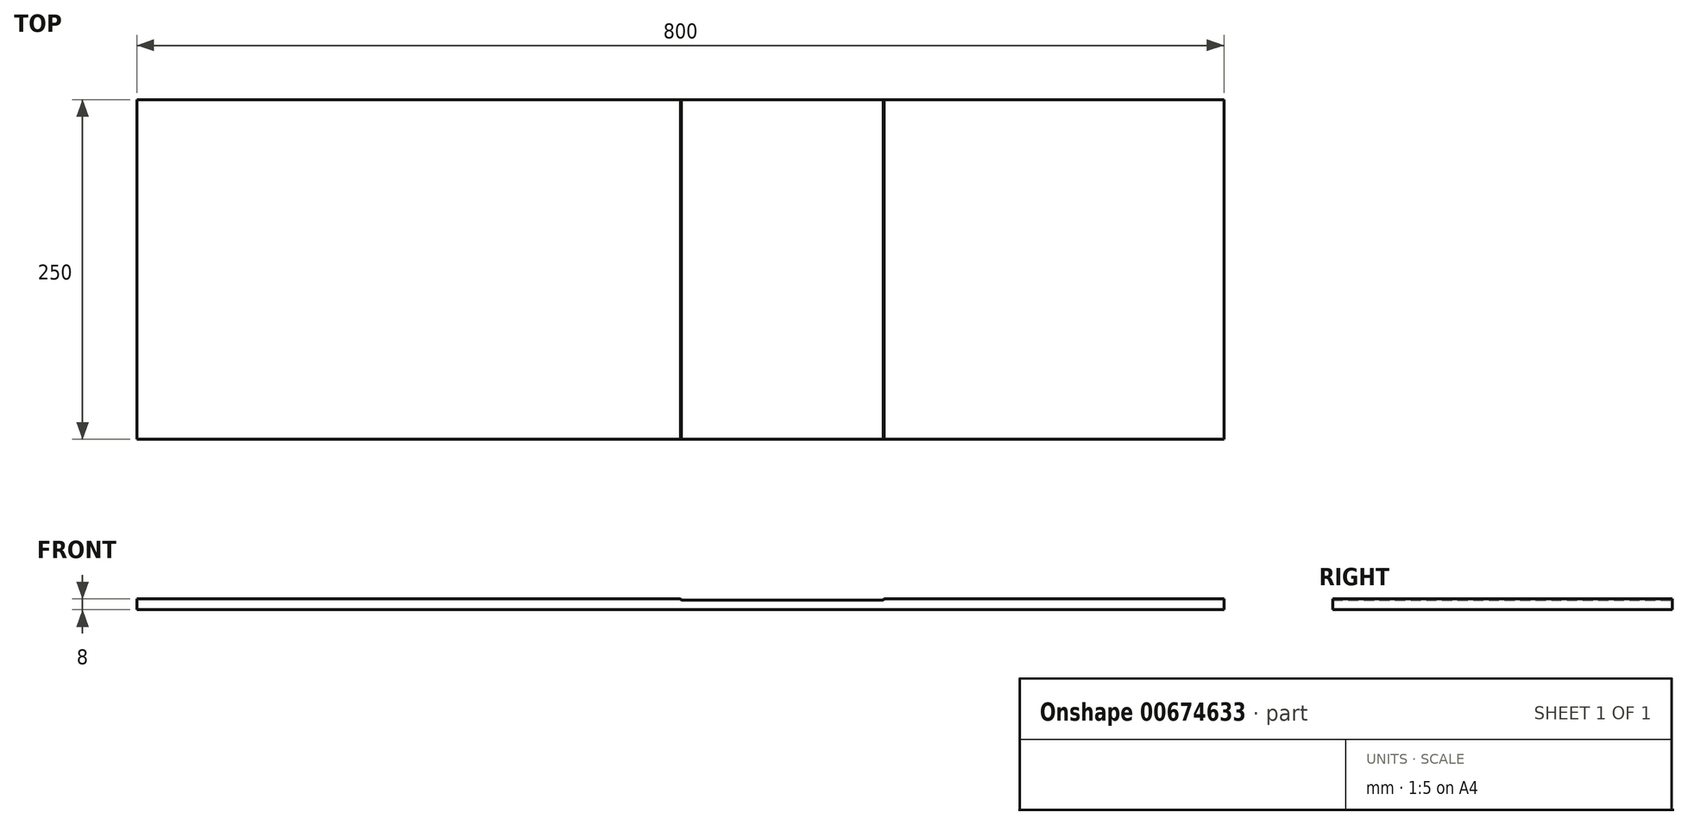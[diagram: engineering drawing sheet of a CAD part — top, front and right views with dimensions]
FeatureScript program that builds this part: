
annotation { "Feature Type Name" : "Feature", "Feature Type Description" : "" }
export const myFeature = defineFeature(function(context is Context, id is Id, definition is map)
    precondition{}
    {
        {
            var Q0;
            Q0=qCreatedBy(makeId("Front.planeOp"),FACE);
            var sketch = newSketch(context, id + "F0", { "sketchPlane" : qUnion([Q0])});
            skLineSegment(sketch, "E0", {"start": v(-225, 8) * mm, "end": v(575, 8) * mm});
            skLineSegment(sketch, "E1", {"start": v(575, 0) * mm, "end": v(-225, 0) * mm});
            skLineSegment(sketch, "E2", {"start": v(-225, 0) * mm, "end": v(-225, 8) * mm});
            skLineSegment(sketch, "E3", {"start": v(575, 0) * mm, "end": v(575, 8) * mm});
            skPoint(sketch, "E4", {"position": v(0, 0) * mm});
            skPoint(sketch, "E5", {"position": v(0, 8) * mm});
            skSolve(sketch);
        }
        {
            var Q0;
            Q0=qCreatedBy(makeId("Front.planeOp"),FACE);
            var sketch = newSketch(context, id + "F1", { "sketchPlane" : qUnion([Q0])});
            skLineSegment(sketch, "E6", {"start": v(175, 8) * mm, "end": v(175.7, 7) * mm});
            skLineSegment(sketch, "E7", {"start": v(250, 8) * mm, "end": v(175, 8) * mm});
            skLineSegment(sketch, "E8", {"start": v(175.7, 7) * mm, "end": v(250, 7) * mm});
            skLineSegment(sketch, "E9", {"start": v(250, 7) * mm, "end": v(250, 8) * mm, "construction": true});
            skLineSegment(sketch, "E10.MirrorCS", {"start": v(325, 8) * mm, "end": v(324.3, 7) * mm});
            skLineSegment(sketch, "E11.MirrorCS", {"start": v(250, 8) * mm, "end": v(325, 8) * mm});
            skLineSegment(sketch, "E12.MirrorCS", {"start": v(324.3, 7) * mm, "end": v(250, 7) * mm});
            skSolve(sketch);
        }
        {
            var Q0;
            Q0=qSketchRegion(id+"F0",true);
            extrude(context, id + "F2", {"entities" : qUnion([Q0]), "oppositeDirection" : true, "depth" : 250 * mm, "offsetDistance" : 25 * mm, "symmetric" : true});
        }
        {
            var Q0;
            Q0=qSketchRegion(id+"F1",true);
            var Q1;
            Q1=makeQuery(id+"F2.opExtrude","CAP_FACE",FACE,{"disambiguationData":[OSD([sQuery(id+"F0.wireOp",EDGE,"E0"),sQuery(id+"F0.wireOp",EDGE,"E1"),sQuery(id+"F0.wireOp",EDGE,"E2"),sQuery(id+"F0.wireOp",EDGE,"E3")])],"isStart":true});
            extrude(context, id + "F3", {"entities" : qUnion([Q0]), "operationType" : NewBodyOperationType.REMOVE, "endBound" : BoundingType.THROUGH_ALL, "depth" : 25 * mm, "endBoundEntityFace" : qUnion([Q1]), "offsetDistance" : 25 * mm});
        }
        {
            var Q0;
            Q0=qSketchRegion(id+"F1",true);
            extrude(context, id + "F4", {"entities" : qUnion([Q0]), "operationType" : NewBodyOperationType.REMOVE, "endBound" : BoundingType.THROUGH_ALL, "oppositeDirection" : true, "depth" : 25 * mm, "offsetDistance" : 25 * mm});
        }
    });
